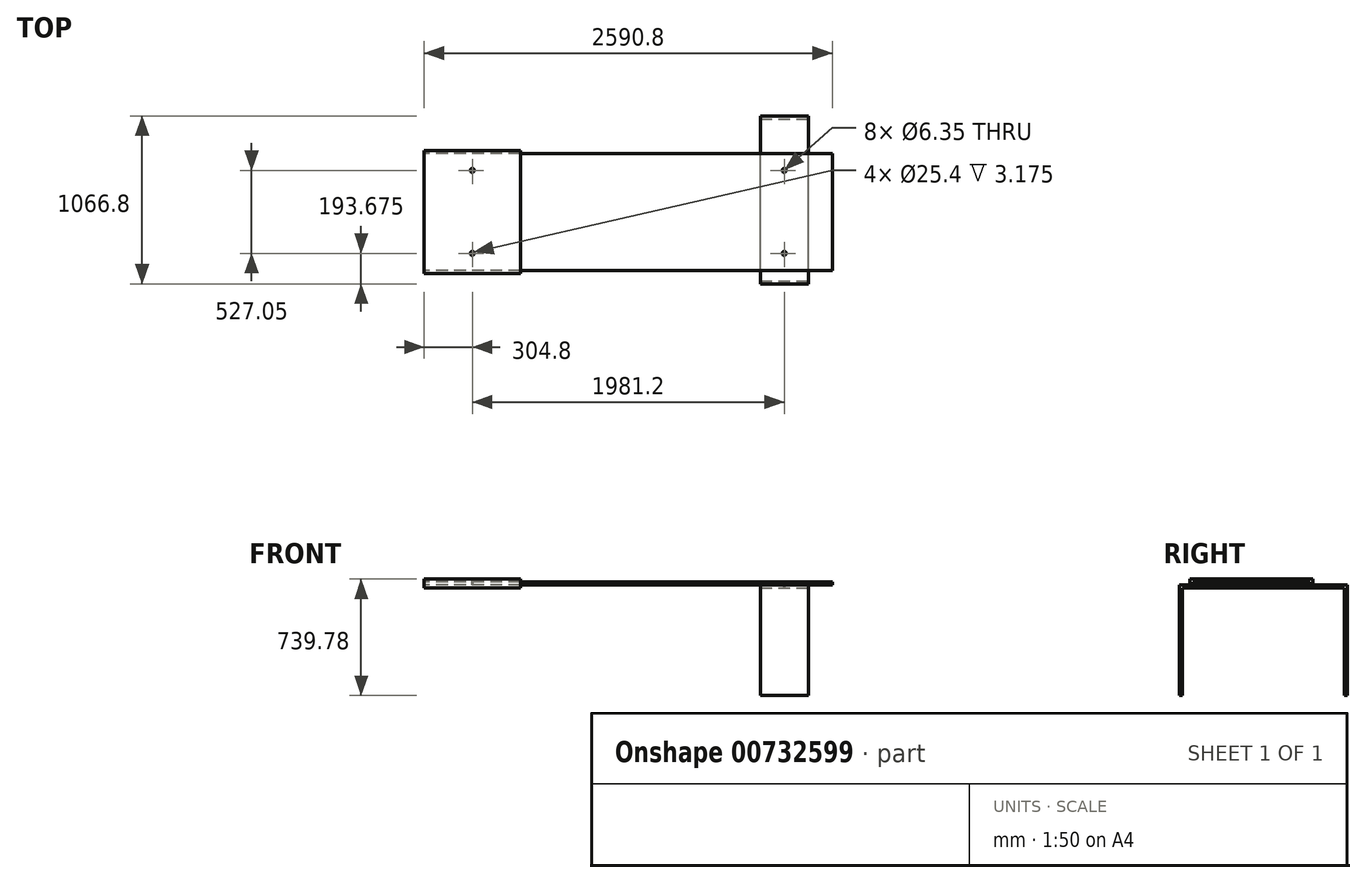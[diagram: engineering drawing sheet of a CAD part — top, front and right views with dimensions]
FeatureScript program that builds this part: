
annotation { "Feature Type Name" : "Feature", "Feature Type Description" : "" }
export const myFeature = defineFeature(function(context is Context, id is Id, definition is map)
    precondition{}
    {
        {
            var Q0;
            Q0=qCreatedBy(makeId("Right.planeOp"),FACE);
            var sketch = newSketch(context, id + "F0", { "sketchPlane" : qUnion([Q0])});
            skLineSegment(sketch, "E0.bottom", {"start": v(390.52, -369.89) * mm, "end": v(-390.53, -369.89) * mm});
            skLineSegment(sketch, "E0.top", {"start": v(390.52, 369.89) * mm, "end": v(-390.53, 369.89) * mm});
            skLineSegment(sketch, "E0.left", {"start": v(390.52, -369.89) * mm, "end": v(390.53, 369.89) * mm});
            skLineSegment(sketch, "E0.right", {"start": v(-390.53, -369.89) * mm, "end": v(-390.53, 369.89) * mm});
            skPoint(sketch, "E0.middle", {"position": v(0, 0) * mm});
            skLineSegment(sketch, "E1.0", {"start": v(371.48, 350.84) * mm, "end": v(-371.48, 350.84) * mm});
            skLineSegment(sketch, "E1.1", {"start": v(371.47, -350.84) * mm, "end": v(371.48, 350.84) * mm});
            skLineSegment(sketch, "E1.2", {"start": v(371.47, -350.84) * mm, "end": v(-371.48, -350.84) * mm});
            skLineSegment(sketch, "E1.3", {"start": v(-371.48, -350.84) * mm, "end": v(-371.48, 350.84) * mm});
            skSolve(sketch);
        }
        {
            var Q0;
            Q0 = qSketchRegion(id + "F0", true);
            extrude(context, id + "F1", {"entities" : qUnion([Q0]), "depth" : 609.6 * mm, "offsetDistance" : 25.4 * mm});
        }
        {
            var Q0;
            Q0=qCreatedBy(makeId("Right.planeOp"),FACE);
            var sketch = newSketch(context, id + "F2", { "sketchPlane" : qUnion([Q0])});
            skLineSegment(sketch, "E2.bottom", {"start": v(-371.48, 350.84) * mm, "end": v(371.48, 350.84) * mm});
            skLineSegment(sketch, "E2.top", {"start": v(-371.48, 331.79) * mm, "end": v(371.48, 331.79) * mm});
            skLineSegment(sketch, "E2.left", {"start": v(-371.48, 350.84) * mm, "end": v(-371.48, 331.79) * mm});
            skLineSegment(sketch, "E2.right", {"start": v(371.48, 350.84) * mm, "end": v(371.48, 331.79) * mm});
            skSolve(sketch);
        }
        {
            var Q0;
            Q0 = qSketchRegion(id + "F2", true);
            extrude(context, id + "F3", {"entities" : qUnion([Q0]), "depth" : 2590.8 * mm, "offsetDistance" : 25.4 * mm});
        }
        {
            var Q0;
            Q0=qCreatedBy(makeId("Front.planeOp"),FACE);
            var sketch = newSketch(context, id + "F4", { "sketchPlane" : qUnion([Q0])});
            skLineSegment(sketch, "E3.bottom", {"start": v(2438.4, 331.79) * mm, "end": v(2133.6, 331.79) * mm});
            skLineSegment(sketch, "E3.top", {"start": v(2438.4, -369.89) * mm, "end": v(2133.6, -369.89) * mm});
            skLineSegment(sketch, "E3.left", {"start": v(2438.4, 331.79) * mm, "end": v(2438.4, -369.89) * mm});
            skLineSegment(sketch, "E3.right", {"start": v(2133.6, 331.79) * mm, "end": v(2133.6, -369.89) * mm});
            skLineSegment(sketch, "E4", {"start": v(2133.6, -369.89) * mm, "end": v(609.6, -369.89) * mm, "construction": true});
            skSolve(sketch);
        }
        {
            var Q0;
            Q0 = qSketchRegion(id + "F4", true);
            extrude(context, id + "F5", {"entities" : qUnion([Q0]), "depth" : 457.2 * mm, "offsetDistance" : 25.4 * mm, "hasSecondDirection" : true, "secondDirectionOppositeDirection" : true, "secondDirectionDepth" : 609.6 * mm});
        }
        {
            var Q0;
            Q0=makeQuery(id+"F5.opExtrude","SWEPT_FACE",FACE,{"disambiguationData":[OSD([sQuery(id+"F4.wireOp",EDGE,"E3.left")])]});
            var sketch = newSketch(context, id + "F6", { "sketchPlane" : qUnion([Q0])});
            skLineSegment(sketch, "E5.bottom", {"start": v(-438.15, -369.89) * mm, "end": v(590.55, -369.89) * mm});
            skLineSegment(sketch, "E5.top", {"start": v(-438.15, 312.74) * mm, "end": v(590.55, 312.74) * mm});
            skLineSegment(sketch, "E5.left", {"start": v(-438.15, -369.89) * mm, "end": v(-438.15, 312.74) * mm});
            skLineSegment(sketch, "E5.right", {"start": v(590.55, -369.89) * mm, "end": v(590.55, 312.74) * mm});
            skSolve(sketch);
        }
        {
            var Q0;
            Q0 = qSketchRegion(id + "F6", true);
            extrude(context, id + "F7", {"entities" : qUnion([Q0]), "operationType" : NewBodyOperationType.REMOVE, "endBound" : BoundingType.THROUGH_ALL, "oppositeDirection" : true, "depth" : 25.4 * mm, "offsetDistance" : 25.4 * mm});
        }
        {
            var Q0;
            Q0=makeQuery(id+"F1.opExtrude","SWEPT_FACE",FACE,{"disambiguationData":[OSD([sQuery(id+"F0.wireOp",EDGE,"E0.top")])]});
            var sketch = newSketch(context, id + "F8", { "sketchPlane" : qUnion([Q0])});
            skLineSegment(sketch, "E6", {"start": v(304.8, 390.53) * mm, "end": v(304.8, -390.53) * mm, "construction": true});
            skCircle(sketch, "E7", {"center": v(304.8, 263.53) * mm, "radius": 12.7 * mm});
            skCircle(sketch, "E8", {"center": v(304.8, -263.53) * mm, "radius": 12.7 * mm});
            skSolve(sketch);
        }
        {
            var Q0;
            Q0 = qSketchRegion(id + "F8", true);
            var Q1;
            Q1=sQuery(id+"F8.wireOp",EDGE,"E7");
            var Q2;
            Q2=sQuery(id+"F8.wireOp",EDGE,"E8");
            extrude(context, id + "F9", {"entities" : qUnion([Q0]), "operationType" : NewBodyOperationType.REMOVE, "surfaceOperationType" : NewSurfaceOperationType.ADD, "surfaceEntities" : qUnion([Q1, Q2]), "oppositeDirection" : true, "depth" : 3.17 * mm, "offsetDistance" : 25.4 * mm});
        }
        {
            var Q0;
            Q0=makeQuery(id+"F3.opExtrude","SWEPT_FACE",FACE,{"disambiguationData":[OSD([sQuery(id+"F2.wireOp",EDGE,"E2.bottom")])]});
            var sketch = newSketch(context, id + "F10", { "sketchPlane" : qUnion([Q0])});
            skLineSegment(sketch, "E9", {"start": v(2286, 371.48) * mm, "end": v(2286, -457.2) * mm, "construction": true});
            skCircle(sketch, "E10", {"center": v(2286, -263.53) * mm, "radius": 12.7 * mm});
            skCircle(sketch, "E11", {"center": v(2286, 263.53) * mm, "radius": 12.7 * mm});
            skSolve(sketch);
        }
        {
            var Q0;
            Q0 = qSketchRegion(id + "F10", true);
            extrude(context, id + "F11", {"entities" : qUnion([Q0]), "operationType" : NewBodyOperationType.REMOVE, "oppositeDirection" : true, "depth" : 3.17 * mm, "offsetDistance" : 25.4 * mm});
        }
        {
            var Q0;
            Q0=makeQuery(id+"F11.boolean.opBoolean","COPY",FACE,{"derivedFrom":makeQuery(id+"F11.opExtrude","CAP_FACE",FACE,{"disambiguationData":[OSD([sQuery(id+"F10.wireOp",EDGE,"E11")])],"isStart":false})});
            var sketch = newSketch(context, id + "F12", { "sketchPlane" : qUnion([Q0])});
            skCircle(sketch, "E12", {"center": v(2286, 263.53) * mm, "radius": 3.18 * mm});
            skSolve(sketch);
        }
        {
            var Q0;
            Q0 = qSketchRegion(id + "F12", true);
            extrude(context, id + "F13", {"entities" : qUnion([Q0]), "operationType" : NewBodyOperationType.REMOVE, "endBound" : BoundingType.THROUGH_ALL, "oppositeDirection" : true, "depth" : 25.4 * mm, "offsetDistance" : 25.4 * mm});
        }
        {
            var Q0;
            Q0=makeQuery(id+"F11.boolean.opBoolean","COPY",FACE,{"derivedFrom":makeQuery(id+"F11.opExtrude","CAP_FACE",FACE,{"disambiguationData":[OSD([sQuery(id+"F10.wireOp",EDGE,"E10")])],"isStart":false})});
            var sketch = newSketch(context, id + "F14", { "sketchPlane" : qUnion([Q0])});
            skCircle(sketch, "E13", {"center": v(2286, -263.53) * mm, "radius": 3.18 * mm});
            skSolve(sketch);
        }
        {
            var Q0;
            Q0 = qSketchRegion(id + "F14", true);
            extrude(context, id + "F15", {"entities" : qUnion([Q0]), "operationType" : NewBodyOperationType.REMOVE, "endBound" : BoundingType.THROUGH_ALL, "oppositeDirection" : true, "depth" : 25.4 * mm, "offsetDistance" : 25.4 * mm});
        }
        {
            var Q0;
            Q0=makeQuery(id+"F9.boolean.opBoolean","COPY",FACE,{"derivedFrom":makeQuery(id+"F9.opExtrude","CAP_FACE",FACE,{"disambiguationData":[OSD([sQuery(id+"F8.wireOp",EDGE,"E7")])],"isStart":false})});
            var sketch = newSketch(context, id + "F16", { "sketchPlane" : qUnion([Q0])});
            skCircle(sketch, "E14", {"center": v(304.8, 263.53) * mm, "radius": 3.18 * mm});
            skSolve(sketch);
        }
        {
            var Q0;
            Q0 = qSketchRegion(id + "F16", true);
            extrude(context, id + "F17", {"entities" : qUnion([Q0]), "operationType" : NewBodyOperationType.REMOVE, "oppositeDirection" : true, "depth" : 127 * mm, "offsetDistance" : 25.4 * mm});
        }
        {
            var Q0;
            Q0=makeQuery(id+"F9.boolean.opBoolean","COPY",FACE,{"derivedFrom":makeQuery(id+"F9.opExtrude","CAP_FACE",FACE,{"disambiguationData":[OSD([sQuery(id+"F8.wireOp",EDGE,"E8")])],"isStart":false})});
            var sketch = newSketch(context, id + "F18", { "sketchPlane" : qUnion([Q0])});
            skSolve(sketch);
        }
        {
            var Q0;
            Q0=makeQuery(id+"F18.imprint","IMPRINT",FACE,{"disambiguationData":[TD([[makeQuery(id+"F18.imprint","IMPRINT",EDGE,{"derivedFrom":makeQuery(id+"F9.boolean.opBoolean","COPY",EDGE,{"derivedFrom":makeQuery(id+"F9.opExtrude","CAP_EDGE",EDGE,{"disambiguationData":[OSD([sQuery(id+"F8.wireOp",EDGE,"E8")])],"isStart":false})})}),1.0]])]});
            var sketch = newSketch(context, id + "F19", { "sketchPlane" : qUnion([Q0])});
            skCircle(sketch, "E15", {"center": v(304.8, -263.53) * mm, "radius": 3.18 * mm});
            skSolve(sketch);
        }
        {
            var Q0;
            Q0 = qSketchRegion(id + "F19", true);
            extrude(context, id + "F20", {"entities" : qUnion([Q0]), "operationType" : NewBodyOperationType.REMOVE, "oppositeDirection" : true, "depth" : 317.5 * mm, "offsetDistance" : 25.4 * mm});
        }
    });
